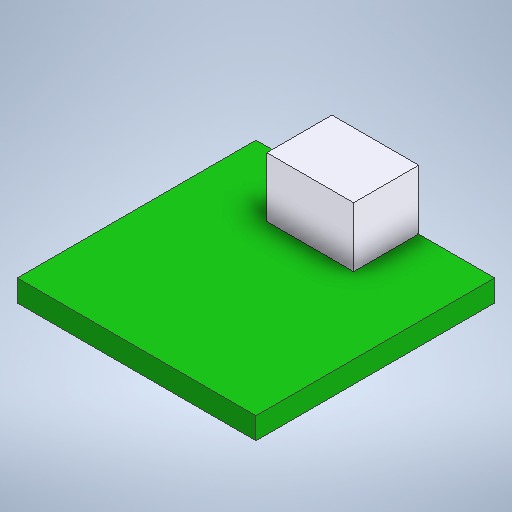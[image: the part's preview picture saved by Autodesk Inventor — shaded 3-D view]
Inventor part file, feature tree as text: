
AUTODESK INVENTOR PART (.ipt)
format: ipt  version: 2025.2 (Build 292293000, 293)  size: 245,760 bytes
history: native  units: mm
features: extrude x3, sketch x3
ambient origin geometry x8: Origin, YZ Plane, XZ Plane, XY Plane, X Axis, Y Axis, Z Axis, Center Point
bodies: Solid1 (feature_tree)
feature tree (6):
  extrude  "Extrusion1"  Depth=22.0mm
  extrude  "Extrusion2"  Depth=8.0mm
  extrude  "Extrusion3"  Depth=7.0mm
  sketch  "Sketch1"  dims[d0=22.0mm d1=22.0mm]
  sketch  "Sketch2"  dims[d2=2.0mm d3=0.0mm d4=8.0mm]
  sketch  "Sketch3"  dims[d5=7.0mm d6=7.0mm d7=6.0mm d8=5.5mm d9=0.0mm d10=0.1mm d11=0.1mm d12=0.0mm]
